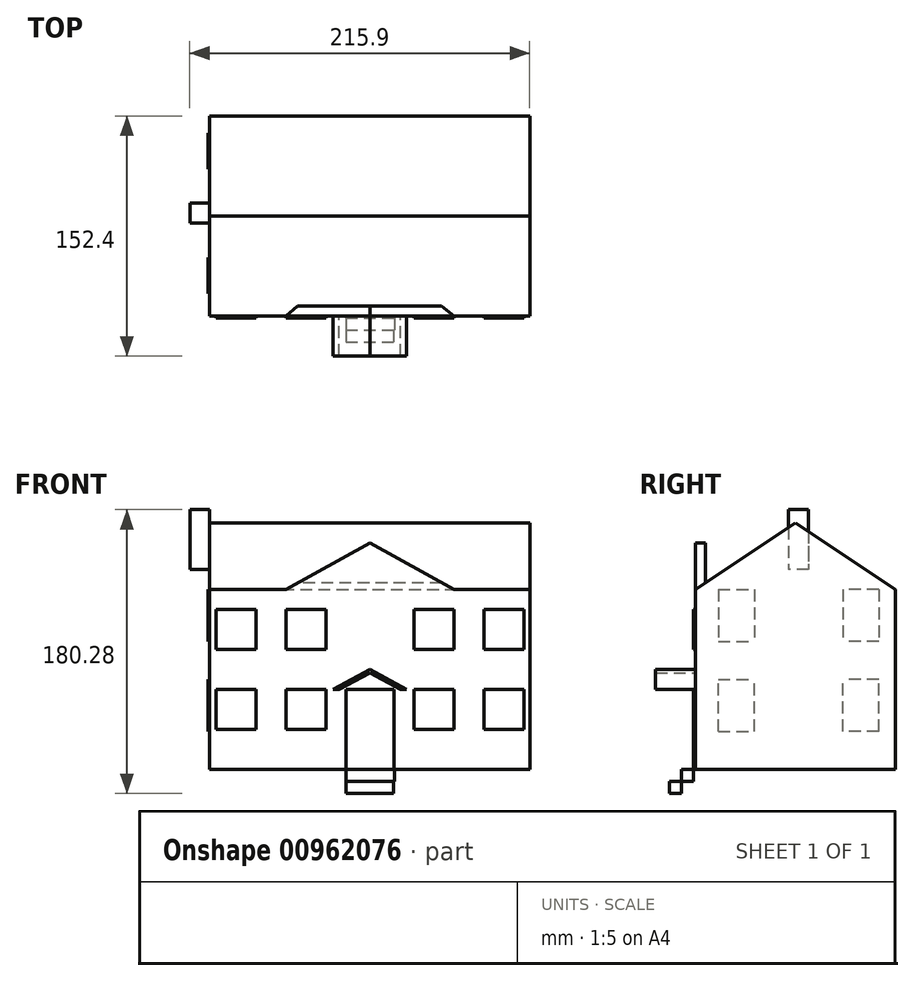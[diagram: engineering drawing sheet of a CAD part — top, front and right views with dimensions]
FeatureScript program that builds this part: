
annotation { "Feature Type Name" : "Feature", "Feature Type Description" : "" }
export const myFeature = defineFeature(function(context is Context, id is Id, definition is map)
    precondition{}
    {
        {
            var Q0;
            Q0=qCreatedBy(makeId("Front.planeOp"),FACE);
            var sketch = newSketch(context, id + "F0", { "sketchPlane" : qUnion([Q0])});
            skLineSegment(sketch, "E0.bottom", {"start": v(-112.8, 58.9) * mm, "end": v(90.4, 58.9) * mm});
            skLineSegment(sketch, "E0.top", {"start": v(-112.8, -55.4) * mm, "end": v(90.4, -55.4) * mm});
            skLineSegment(sketch, "E0.left", {"start": v(-112.8, 58.9) * mm, "end": v(-112.8, -55.4) * mm});
            skLineSegment(sketch, "E0.right", {"start": v(90.4, 58.9) * mm, "end": v(90.4, -55.4) * mm});
            skSolve(sketch);
        }
        {
            var Q0;
            Q0 = qSketchRegion(id + "F0", true);
            extrude(context, id + "F1", {"entities" : qUnion([Q0]), "depth" : 127 * mm, "offsetDistance" : 25.4 * mm});
        }
        {
            var Q0;
            Q0=makeQuery(id+"F1.opExtrude","SWEPT_FACE",FACE,{"disambiguationData":[OSD([sQuery(id+"F0.wireOp",EDGE,"E0.right")])]});
            var sketch = newSketch(context, id + "F2", { "sketchPlane" : qUnion([Q0])});
            skLineSegment(sketch, "E1", {"start": v(-63.5, 58.9) * mm, "end": v(-63.5, -55.4) * mm});
            skLineSegment(sketch, "E2", {"start": v(-127, 58.9) * mm, "end": v(-63.5, 101.01) * mm});
            skLineSegment(sketch, "E3", {"start": v(-63.5, 101.01) * mm, "end": v(0, 58.9) * mm});
            skLineSegment(sketch, "E4", {"start": v(-127, 58.9) * mm, "end": v(0, 58.9) * mm});
            skSolve(sketch);
        }
        {
            var Q0;
            {var subQ0=sQuery(id+"F2.wireOp",EDGE,"E2");Q0=makeQuery(id+"F2.imprint","IMPRINT",FACE,{"disambiguationData":[TD([[makeQuery(id+"F2.imprint","IMPRINT",EDGE,{"derivedFrom":subQ0}),-1.0]])]});}
            extrude(context, id + "F3", {"entities" : qUnion([Q0]), "operationType" : NewBodyOperationType.ADD, "oppositeDirection" : true, "depth" : 203.2 * mm, "offsetDistance" : 25.4 * mm});
        }
        {
            var Q0;
            Q0=makeQuery(id+"F1.opExtrude","CAP_FACE",FACE,{"disambiguationData":[OSD([sQuery(id+"F0.wireOp",EDGE,"E0.bottom"),sQuery(id+"F0.wireOp",EDGE,"E0.top"),sQuery(id+"F0.wireOp",EDGE,"E0.left"),sQuery(id+"F0.wireOp",EDGE,"E0.right")])],"isStart":false});
            var sketch = newSketch(context, id + "F4", { "sketchPlane" : qUnion([Q0])});
            skLineSegment(sketch, "E5.bottom", {"start": v(-26.44, -55.4) * mm, "end": v(4.04, -55.4) * mm});
            skLineSegment(sketch, "E5.top", {"start": v(-26.44, -4.6) * mm, "end": v(4.04, -4.6) * mm});
            skLineSegment(sketch, "E5.left", {"start": v(-26.44, -55.4) * mm, "end": v(-26.44, -4.6) * mm});
            skLineSegment(sketch, "E5.right", {"start": v(4.04, -55.4) * mm, "end": v(4.04, -4.6) * mm});
            skSolve(sketch);
        }
        {
            var Q0;
            Q0 = qSketchRegion(id + "F4", true);
            extrude(context, id + "F5", {"entities" : qUnion([Q0]), "operationType" : NewBodyOperationType.ADD, "depth" : 1.27 * mm, "offsetDistance" : 25.4 * mm});
        }
        {
            var Q0;
            Q0=makeQuery(id+"F1.opExtrude","CAP_FACE",FACE,{"disambiguationData":[OSD([sQuery(id+"F0.wireOp",EDGE,"E0.bottom"),sQuery(id+"F0.wireOp",EDGE,"E0.top"),sQuery(id+"F0.wireOp",EDGE,"E0.left"),sQuery(id+"F0.wireOp",EDGE,"E0.right")])],"isStart":false});
            var sketch = newSketch(context, id + "F6", { "sketchPlane" : qUnion([Q0])});
            skLineSegment(sketch, "E6.bottom", {"start": v(-108.99, -4.6) * mm, "end": v(-83.59, -4.6) * mm});
            skLineSegment(sketch, "E6.top", {"start": v(-108.99, -30.02) * mm, "end": v(-83.59, -30.02) * mm});
            skLineSegment(sketch, "E6.left", {"start": v(-108.99, -4.6) * mm, "end": v(-108.99, -30.02) * mm});
            skLineSegment(sketch, "E6.right", {"start": v(-83.59, -4.6) * mm, "end": v(-83.59, -30.02) * mm});
            skLineSegment(sketch, "E7.bottom", {"start": v(-64.54, -4.6) * mm, "end": v(-39.14, -4.6) * mm});
            skLineSegment(sketch, "E7.top", {"start": v(-64.54, -30.02) * mm, "end": v(-39.14, -30.02) * mm});
            skLineSegment(sketch, "E7.left", {"start": v(-64.54, -4.6) * mm, "end": v(-64.54, -30.02) * mm});
            skLineSegment(sketch, "E7.right", {"start": v(-39.14, -4.6) * mm, "end": v(-39.14, -30.02) * mm});
            skLineSegment(sketch, "E8.MirrorCS", {"start": v(86.6, -30.02) * mm, "end": v(61.2, -30.02) * mm});
            skLineSegment(sketch, "E9.MirrorCS", {"start": v(86.6, -4.6) * mm, "end": v(61.2, -4.6) * mm});
            skLineSegment(sketch, "E10.MirrorCS", {"start": v(16.74, -4.6) * mm, "end": v(16.74, -30.02) * mm});
            skLineSegment(sketch, "E11.MirrorCS", {"start": v(86.6, -4.6) * mm, "end": v(86.6, -30.02) * mm});
            skLineSegment(sketch, "E12.MirrorCS", {"start": v(42.14, -30.02) * mm, "end": v(16.74, -30.02) * mm});
            skLineSegment(sketch, "E13.MirrorCS", {"start": v(61.2, -4.6) * mm, "end": v(61.2, -30.02) * mm});
            skLineSegment(sketch, "E14.MirrorCS", {"start": v(42.14, -4.6) * mm, "end": v(42.14, -30.02) * mm});
            skLineSegment(sketch, "E15.MirrorCS", {"start": v(42.14, -4.6) * mm, "end": v(16.74, -4.6) * mm});
            skLineSegment(sketch, "E16.MirrorCS", {"start": v(42.14, 46.2) * mm, "end": v(16.74, 46.2) * mm});
            skLineSegment(sketch, "E17.MirrorCS", {"start": v(-108.99, 46.2) * mm, "end": v(-83.59, 46.2) * mm});
            skLineSegment(sketch, "E18.MirrorCS", {"start": v(86.6, 20.8) * mm, "end": v(61.2, 20.8) * mm});
            skLineSegment(sketch, "E19.MirrorCS", {"start": v(42.14, 20.8) * mm, "end": v(42.14, 46.2) * mm});
            skLineSegment(sketch, "E20.MirrorCS", {"start": v(-83.59, 20.8) * mm, "end": v(-83.59, 46.2) * mm});
            skLineSegment(sketch, "E21.MirrorCS", {"start": v(86.6, 20.8) * mm, "end": v(86.6, 46.2) * mm});
            skLineSegment(sketch, "E22.MirrorCS", {"start": v(-108.99, 20.8) * mm, "end": v(-83.59, 20.8) * mm});
            skLineSegment(sketch, "E23.MirrorCS", {"start": v(-64.54, 46.2) * mm, "end": v(-39.14, 46.2) * mm});
            skLineSegment(sketch, "E24.MirrorCS", {"start": v(16.74, 20.8) * mm, "end": v(16.74, 46.2) * mm});
            skLineSegment(sketch, "E25.MirrorCS", {"start": v(-108.99, 20.8) * mm, "end": v(-108.99, 46.2) * mm});
            skLineSegment(sketch, "E26.MirrorCS", {"start": v(-64.54, 20.8) * mm, "end": v(-39.14, 20.8) * mm});
            skLineSegment(sketch, "E27.MirrorCS", {"start": v(42.14, 20.8) * mm, "end": v(16.74, 20.8) * mm});
            skLineSegment(sketch, "E28.MirrorCS", {"start": v(61.2, 20.8) * mm, "end": v(61.2, 46.2) * mm});
            skLineSegment(sketch, "E29.MirrorCS", {"start": v(-39.14, 20.8) * mm, "end": v(-39.14, 46.2) * mm});
            skLineSegment(sketch, "E30.MirrorCS", {"start": v(-64.54, 20.8) * mm, "end": v(-64.54, 46.2) * mm});
            skLineSegment(sketch, "E31.MirrorCS", {"start": v(86.6, 46.2) * mm, "end": v(61.2, 46.2) * mm});
            skSolve(sketch);
        }
        {
            var Q0;
            Q0=makeQuery(id+"F6.imprint","IMPRINT",FACE,{"disambiguationData":[TD([[makeQuery(id+"F6.imprint","IMPRINT",EDGE,{"derivedFrom":sQuery(id+"F6.wireOp",EDGE,"E17.MirrorCS")}),-1.0]])]});
            var Q1;
            Q1=makeQuery(id+"F6.imprint","IMPRINT",FACE,{"disambiguationData":[TD([[makeQuery(id+"F6.imprint","IMPRINT",EDGE,{"derivedFrom":sQuery(id+"F6.wireOp",EDGE,"E23.MirrorCS")}),-1.0]])]});
            var Q2;
            Q2=makeQuery(id+"F6.imprint","IMPRINT",FACE,{"disambiguationData":[TD([[makeQuery(id+"F6.imprint","IMPRINT",EDGE,{"derivedFrom":sQuery(id+"F6.wireOp",EDGE,"E16.MirrorCS")}),1.0]])]});
            var Q3;
            Q3=makeQuery(id+"F6.imprint","IMPRINT",FACE,{"disambiguationData":[TD([[makeQuery(id+"F6.imprint","IMPRINT",EDGE,{"derivedFrom":sQuery(id+"F6.wireOp",EDGE,"E18.MirrorCS")}),-1.0]])]});
            var Q4;
            Q4=makeQuery(id+"F6.imprint","IMPRINT",FACE,{"disambiguationData":[TD([[makeQuery(id+"F6.imprint","IMPRINT",EDGE,{"derivedFrom":sQuery(id+"F6.wireOp",EDGE,"E8.MirrorCS")}),-1.0]])]});
            var Q5;
            Q5=makeQuery(id+"F6.imprint","IMPRINT",FACE,{"disambiguationData":[TD([[makeQuery(id+"F6.imprint","IMPRINT",EDGE,{"derivedFrom":sQuery(id+"F6.wireOp",EDGE,"E10.MirrorCS")}),1.0]])]});
            var Q6;
            Q6=makeQuery(id+"F6.imprint","IMPRINT",FACE,{"disambiguationData":[TD([[makeQuery(id+"F6.imprint","IMPRINT",EDGE,{"derivedFrom":sQuery(id+"F6.wireOp",EDGE,"E7.bottom")}),-1.0]])]});
            var Q7;
            Q7=makeQuery(id+"F6.imprint","IMPRINT",FACE,{"disambiguationData":[TD([[makeQuery(id+"F6.imprint","IMPRINT",EDGE,{"derivedFrom":sQuery(id+"F6.wireOp",EDGE,"E6.bottom")}),-1.0]])]});
            extrude(context, id + "F7", {"entities" : qUnion([Q0, Q1, Q2, Q3, Q4, Q5, Q6, Q7]), "operationType" : NewBodyOperationType.ADD, "depth" : 1.27 * mm, "offsetDistance" : 25.4 * mm});
        }
        {
            var Q0;
            Q0=makeQuery(id+"F1.opExtrude","CAP_FACE",FACE,{"disambiguationData":[OSD([sQuery(id+"F0.wireOp",EDGE,"E0.bottom"),sQuery(id+"F0.wireOp",EDGE,"E0.top"),sQuery(id+"F0.wireOp",EDGE,"E0.left"),sQuery(id+"F0.wireOp",EDGE,"E0.right")])],"isStart":false});
            var sketch = newSketch(context, id + "F8", { "sketchPlane" : qUnion([Q0])});
            skLineSegment(sketch, "E32", {"start": v(-34.57, -4.6) * mm, "end": v(-30.76, -4.6) * mm});
            skLineSegment(sketch, "E33", {"start": v(-11.2, -4.6) * mm, "end": v(-11.2, 8.1) * mm});
            skLineSegment(sketch, "E34", {"start": v(-34.57, -4.6) * mm, "end": v(-11.2, 8.1) * mm});
            skLineSegment(sketch, "E35", {"start": v(-30.76, -4.6) * mm, "end": v(-11.2, 6.02) * mm});
            skPoint(sketch, "E35.endSnap0", {"position": v(-11.2, 1.74) * mm});
            skLineSegment(sketch, "E36", {"start": v(-11.2, 6.02) * mm, "end": v(8.36, -4.6) * mm});
            skLineSegment(sketch, "E37", {"start": v(8.36, -4.6) * mm, "end": v(12.17, -4.6) * mm});
            skLineSegment(sketch, "E38", {"start": v(12.17, -4.6) * mm, "end": v(-11.2, 8.1) * mm});
            skSolve(sketch);
        }
        {
            var Q0;
            Q0=makeQuery(id+"F8.imprint","IMPRINT",FACE,{"disambiguationData":[TD([[makeQuery(id+"F8.imprint","IMPRINT",EDGE,{"derivedFrom":sQuery(id+"F8.wireOp",EDGE,"E32")}),1.0]])]});
            var Q1;
            {var subQ2=sQuery(id+"F8.wireOp",EDGE,"E36");Q1=makeQuery(id+"F8.imprint","IMPRINT",FACE,{"disambiguationData":[TD([[makeQuery(id+"F8.imprint","IMPRINT",EDGE,{"derivedFrom":subQ2}),1.0]])]});}
            extrude(context, id + "F9", {"entities" : qUnion([Q0, Q1]), "operationType" : NewBodyOperationType.ADD, "depth" : 25.4 * mm, "offsetDistance" : 25.4 * mm});
        }
        {
            var Q0;
            Q0=makeQuery(id+"F3.boolean.opBoolean","MERGE",FACE,{"derivedFrom":[makeQuery(id+"F1.opExtrude","SWEPT_FACE",FACE,{"disambiguationData":[OSD([sQuery(id+"F0.wireOp",EDGE,"E0.left")])]}),makeQuery(id+"F3.opExtrude","CAP_FACE",FACE,{"disambiguationData":[OSD([sQuery(id+"F2.wireOp",EDGE,"E2"),sQuery(id+"F2.wireOp",EDGE,"E3"),sQuery(id+"F2.wireOp",EDGE,"E4")])],"isStart":false})]});
            var sketch = newSketch(context, id + "F10", { "sketchPlane" : qUnion([Q0])});
            skLineSegment(sketch, "E39.bottom", {"start": v(55.29, 84.23) * mm, "end": v(67.99, 84.23) * mm});
            skLineSegment(sketch, "E39.top", {"start": v(55.29, 71.53) * mm, "end": v(67.99, 71.53) * mm});
            skLineSegment(sketch, "E39.left", {"start": v(55.29, 84.23) * mm, "end": v(55.29, 71.53) * mm});
            skLineSegment(sketch, "E39.right", {"start": v(67.99, 84.23) * mm, "end": v(67.99, 71.53) * mm});
            skSolve(sketch);
        }
        {
            var Q0;
            Q0=makeQuery(id+"F10.imprint","IMPRINT",FACE,{"disambiguationData":[TD([[makeQuery(id+"F10.imprint","IMPRINT",EDGE,{"derivedFrom":sQuery(id+"F10.wireOp",EDGE,"E39.bottom")}),-1.0]])]});
            extrude(context, id + "F11", {"entities" : qUnion([Q0]), "operationType" : NewBodyOperationType.ADD, "depth" : 12.7 * mm, "offsetDistance" : 25.4 * mm});
        }
        {
            var Q0;
            Q0=makeQuery(id+"F11.opExtrude","SWEPT_FACE",FACE,{"disambiguationData":[OSD([sQuery(id+"F10.wireOp",EDGE,"E39.bottom")])]});
            var sketch = newSketch(context, id + "F12", { "sketchPlane" : qUnion([Q0])});
            skLineSegment(sketch, "E40.bottom", {"start": v(-125.5, -67.99) * mm, "end": v(-112.8, -67.99) * mm});
            skLineSegment(sketch, "E40.top", {"start": v(-125.5, -55.29) * mm, "end": v(-112.8, -55.29) * mm});
            skLineSegment(sketch, "E40.left", {"start": v(-125.5, -67.99) * mm, "end": v(-125.5, -55.29) * mm});
            skLineSegment(sketch, "E40.right", {"start": v(-112.8, -67.99) * mm, "end": v(-112.8, -55.29) * mm});
            skSolve(sketch);
        }
        {
            var Q0;
            Q0 = qSketchRegion(id + "F12", true);
            extrude(context, id + "F13", {"entities" : qUnion([Q0]), "operationType" : NewBodyOperationType.ADD, "depth" : 25.4 * mm, "offsetDistance" : 25.4 * mm});
        }
        {
            var Q0;
            Q0=makeQuery(id+"F5.boolean.opBoolean","MERGE",FACE,{"derivedFrom":[makeQuery(id+"F1.opExtrude","SWEPT_FACE",FACE,{"disambiguationData":[OSD([sQuery(id+"F0.wireOp",EDGE,"E0.top")])]}),makeQuery(id+"F5.opExtrude","SWEPT_FACE",FACE,{"disambiguationData":[OSD([sQuery(id+"F4.wireOp",EDGE,"E5.bottom")])]})]});
            var sketch = newSketch(context, id + "F14", { "sketchPlane" : qUnion([Q0])});
            skLineSegment(sketch, "E41.bottom", {"start": v(-26.44, 128.27) * mm, "end": v(4.6, 128.27) * mm});
            skLineSegment(sketch, "E41.top", {"start": v(-26.44, 135.89) * mm, "end": v(4.6, 135.89) * mm});
            skLineSegment(sketch, "E41.left", {"start": v(-26.44, 128.27) * mm, "end": v(-26.44, 135.89) * mm});
            skLineSegment(sketch, "E41.right", {"start": v(4.6, 128.27) * mm, "end": v(4.6, 135.89) * mm});
            skSolve(sketch);
        }
        {
            var Q0;
            Q0 = qSketchRegion(id + "F14", true);
            extrude(context, id + "F15", {"entities" : qUnion([Q0]), "depth" : 7.62 * mm, "offsetDistance" : 25.4 * mm});
        }
        {
            var Q0;
            Q0=makeQuery(id+"F15.opExtrude","CAP_FACE",FACE,{"disambiguationData":[OSD([sQuery(id+"F14.wireOp",EDGE,"E41.bottom"),sQuery(id+"F14.wireOp",EDGE,"E41.top"),sQuery(id+"F14.wireOp",EDGE,"E41.left"),sQuery(id+"F14.wireOp",EDGE,"E41.right")])],"isStart":false});
            var sketch = newSketch(context, id + "F16", { "sketchPlane" : qUnion([Q0])});
            skLineSegment(sketch, "E42.bottom", {"start": v(-26.44, 135.89) * mm, "end": v(3.98, 135.89) * mm});
            skLineSegment(sketch, "E42.top", {"start": v(-26.44, 143.5) * mm, "end": v(3.98, 143.5) * mm});
            skLineSegment(sketch, "E42.left", {"start": v(-26.44, 135.89) * mm, "end": v(-26.44, 143.5) * mm});
            skLineSegment(sketch, "E42.right", {"start": v(3.98, 135.89) * mm, "end": v(3.98, 143.5) * mm});
            skSolve(sketch);
        }
        {
            var Q0;
            Q0 = qSketchRegion(id + "F16", true);
            extrude(context, id + "F17", {"entities" : qUnion([Q0]), "depth" : 7.62 * mm, "offsetDistance" : 25.4 * mm});
        }
        {
            var Q0;
            Q0=makeQuery(id+"F1.opExtrude","CAP_FACE",FACE,{"disambiguationData":[OSD([sQuery(id+"F0.wireOp",EDGE,"E0.bottom"),sQuery(id+"F0.wireOp",EDGE,"E0.top"),sQuery(id+"F0.wireOp",EDGE,"E0.left"),sQuery(id+"F0.wireOp",EDGE,"E0.right")])],"isStart":false});
            var sketch = newSketch(context, id + "F18", { "sketchPlane" : qUnion([Q0])});
            skLineSegment(sketch, "E43", {"start": v(-64.54, 58.9) * mm, "end": v(-11.2, 88.4) * mm});
            skLineSegment(sketch, "E44", {"start": v(-11.2, 88.4) * mm, "end": v(42.14, 58.9) * mm});
            skLineSegment(sketch, "E45", {"start": v(42.14, 58.9) * mm, "end": v(-64.54, 58.9) * mm});
            skSolve(sketch);
        }
        {
            var Q0;
            Q0 = qSketchRegion(id + "F18", true);
            extrude(context, id + "F19", {"entities" : qUnion([Q0]), "operationType" : NewBodyOperationType.ADD, "oppositeDirection" : true, "depth" : 6.35 * mm, "offsetDistance" : 25.4 * mm});
        }
        {
            var Q0;
            Q0=makeQuery(id+"F3.boolean.opBoolean","MERGE",FACE,{"derivedFrom":[makeQuery(id+"F1.opExtrude","SWEPT_FACE",FACE,{"disambiguationData":[OSD([sQuery(id+"F0.wireOp",EDGE,"E0.left")])]}),makeQuery(id+"F3.opExtrude","CAP_FACE",FACE,{"disambiguationData":[OSD([sQuery(id+"F2.wireOp",EDGE,"E2"),sQuery(id+"F2.wireOp",EDGE,"E3"),sQuery(id+"F2.wireOp",EDGE,"E4")])],"isStart":false})]});
            var sketch = newSketch(context, id + "F20", { "sketchPlane" : qUnion([Q0])});
            skLineSegment(sketch, "E46.bottom", {"start": v(10.63, 58.9) * mm, "end": v(33.5, 58.9) * mm});
            skLineSegment(sketch, "E46.top", {"start": v(10.63, 25.87) * mm, "end": v(33.5, 25.87) * mm});
            skLineSegment(sketch, "E46.left", {"start": v(10.63, 58.9) * mm, "end": v(10.63, 25.87) * mm});
            skLineSegment(sketch, "E46.right", {"start": v(33.5, 58.9) * mm, "end": v(33.5, 25.87) * mm});
            skLineSegment(sketch, "E47.MirrorCS", {"start": v(112.64, 25.87) * mm, "end": v(89.78, 25.87) * mm});
            skLineSegment(sketch, "E48.MirrorCS", {"start": v(112.64, 58.9) * mm, "end": v(112.64, 25.87) * mm});
            skLineSegment(sketch, "E49.MirrorCS", {"start": v(112.64, 58.9) * mm, "end": v(89.78, 58.9) * mm});
            skLineSegment(sketch, "E50.MirrorCS", {"start": v(89.78, 58.9) * mm, "end": v(89.78, 25.87) * mm});
            skLineSegment(sketch, "E51.MirrorCS", {"start": v(112.64, -31.28) * mm, "end": v(112.64, 1.74) * mm});
            skLineSegment(sketch, "E52.MirrorCS", {"start": v(10.63, -31.28) * mm, "end": v(10.63, 1.74) * mm});
            skLineSegment(sketch, "E53.MirrorCS", {"start": v(89.78, -31.28) * mm, "end": v(89.78, 1.74) * mm});
            skLineSegment(sketch, "E54.MirrorCS", {"start": v(33.5, -31.28) * mm, "end": v(33.5, 1.74) * mm});
            skLineSegment(sketch, "E55.MirrorCS", {"start": v(10.63, 1.74) * mm, "end": v(33.5, 1.74) * mm});
            skLineSegment(sketch, "E56.MirrorCS", {"start": v(112.64, 1.74) * mm, "end": v(89.78, 1.74) * mm});
            skLineSegment(sketch, "E57.MirrorCS", {"start": v(10.63, -31.28) * mm, "end": v(33.5, -31.28) * mm});
            skLineSegment(sketch, "E58.MirrorCS", {"start": v(112.64, -31.28) * mm, "end": v(89.78, -31.28) * mm});
            skSolve(sketch);
        }
        {
            var Q0;
            Q0 = qSketchRegion(id + "F20", true);
            extrude(context, id + "F21", {"entities" : qUnion([Q0]), "operationType" : NewBodyOperationType.ADD, "depth" : 1.27 * mm, "offsetDistance" : 25.4 * mm});
        }
    });
